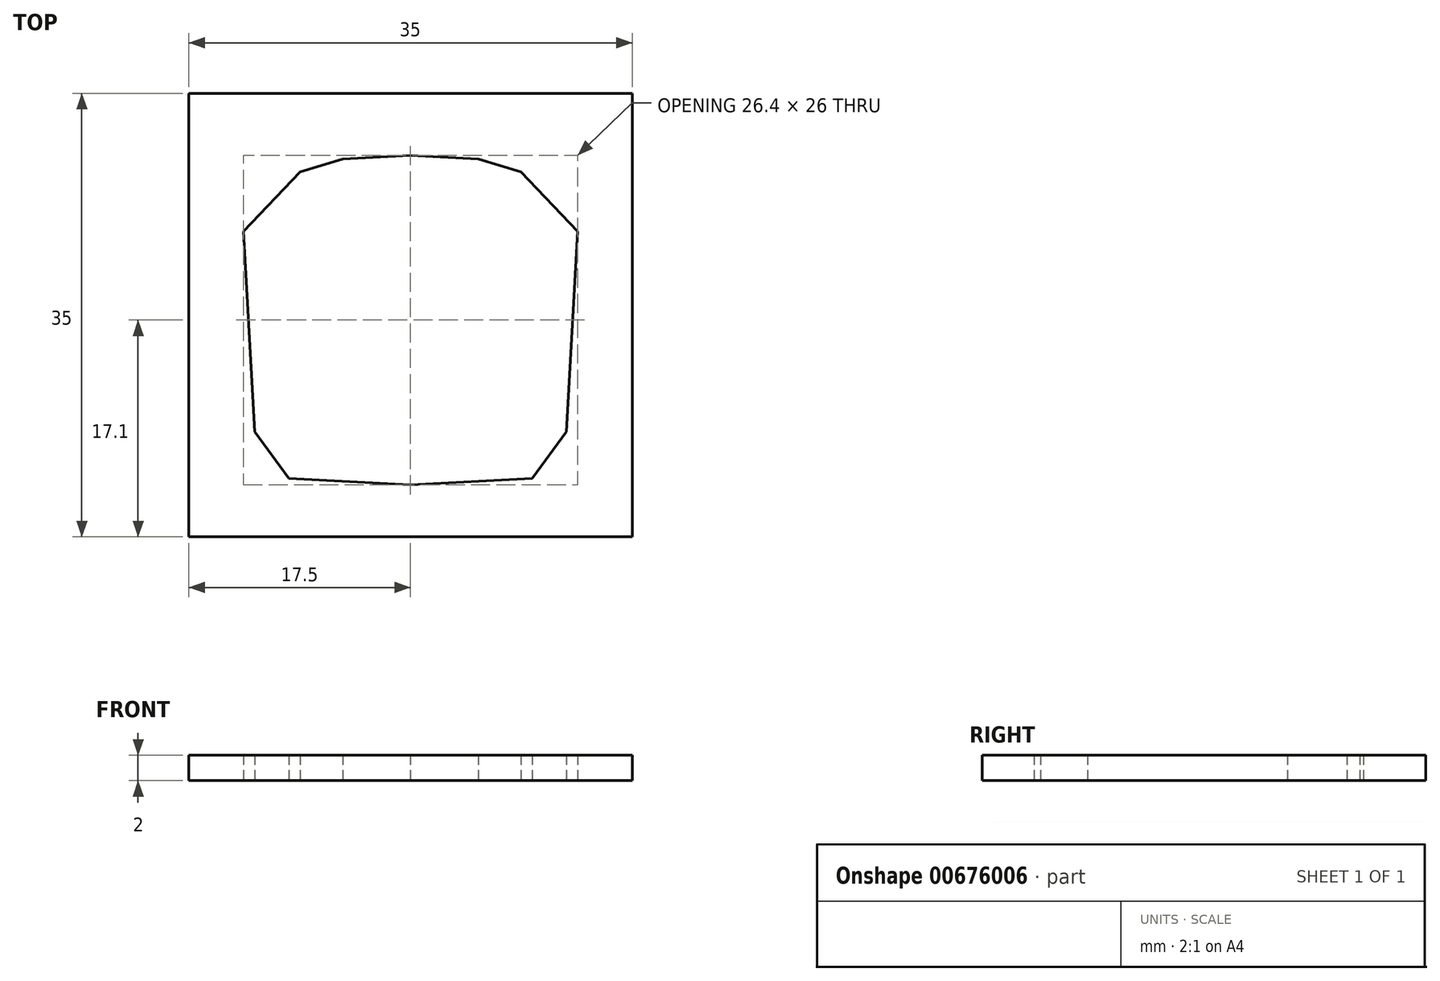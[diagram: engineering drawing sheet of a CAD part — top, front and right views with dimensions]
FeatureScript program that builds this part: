
annotation { "Feature Type Name" : "Feature", "Feature Type Description" : "" }
export const myFeature = defineFeature(function(context is Context, id is Id, definition is map)
    precondition{}
    {
        {
            var Q0;
            Q0=qCreatedBy(makeId("Top.planeOp"),FACE);
            var sketch = newSketch(context, id + "F0", { "sketchPlane" : qUnion([Q0])});
            skPoint(sketch, "E0", {"position": v(9.6, 0.5) * mm});
            skPoint(sketch, "E1", {"position": v(12.3, 4.2) * mm});
            skPoint(sketch, "E2", {"position": v(13.2, 20) * mm});
            skPoint(sketch, "E3", {"position": v(8.7, 24.7) * mm});
            skPoint(sketch, "E4", {"position": v(5.35, 25.7) * mm});
            skPoint(sketch, "E5", {"position": v(0, 26) * mm});
            skLineSegment(sketch, "E6", {"start": v(0, 0) * mm, "end": v(9.6, 0.5) * mm});
            skLineSegment(sketch, "E7", {"start": v(9.6, 0.5) * mm, "end": v(12.3, 4.2) * mm});
            skLineSegment(sketch, "E8", {"start": v(12.3, 4.2) * mm, "end": v(13.2, 20) * mm});
            skLineSegment(sketch, "E9", {"start": v(13.2, 20) * mm, "end": v(8.7, 24.7) * mm});
            skLineSegment(sketch, "E10", {"start": v(8.7, 24.7) * mm, "end": v(5.35, 25.7) * mm});
            skLineSegment(sketch, "E11", {"start": v(5.35, 25.7) * mm, "end": v(0, 26) * mm});
            skLineSegment(sketch, "E12.MirrorCS", {"start": v(-5.35, 25.7) * mm, "end": v(0, 26) * mm});
            skLineSegment(sketch, "E13.MirrorCS", {"start": v(-8.7, 24.7) * mm, "end": v(-5.35, 25.7) * mm});
            skLineSegment(sketch, "E14.MirrorCS", {"start": v(-13.2, 20) * mm, "end": v(-8.7, 24.7) * mm});
            skLineSegment(sketch, "E15.MirrorCS", {"start": v(-12.3, 4.2) * mm, "end": v(-13.2, 20) * mm});
            skLineSegment(sketch, "E16.MirrorCS", {"start": v(-9.6, 0.5) * mm, "end": v(-12.3, 4.2) * mm});
            skLineSegment(sketch, "E17.MirrorCS", {"start": v(0, 0) * mm, "end": v(-9.6, 0.5) * mm});
            skLineSegment(sketch, "E18", {"start": v(0, -4.1) * mm, "end": v(17.5, -4.1) * mm});
            skLineSegment(sketch, "E19", {"start": v(17.5, 30.9) * mm, "end": v(17.5, -4.1) * mm});
            skLineSegment(sketch, "E20", {"start": v(17.5, 30.9) * mm, "end": v(0, 30.9) * mm});
            skLineSegment(sketch, "E21.MirrorCS", {"start": v(-17.5, 30.9) * mm, "end": v(0, 30.9) * mm});
            skLineSegment(sketch, "E22.MirrorCS", {"start": v(-17.5, 30.9) * mm, "end": v(-17.5, -4.1) * mm});
            skLineSegment(sketch, "E23.MirrorCS", {"start": v(0, -4.1) * mm, "end": v(-17.5, -4.1) * mm});
            skSolve(sketch);
        }
        {
            var Q0;
            Q0=makeQuery(id+"F0.imprint","IMPRINT",FACE,{"disambiguationData":[TD([[makeQuery(id+"F0.imprint","IMPRINT",EDGE,{"derivedFrom":sQuery(id+"F0.wireOp",EDGE,"E6")}),-1.0]])]});
            extrude(context, id + "F1", {"entities" : qUnion([Q0]), "depth" : 2 * mm, "offsetDistance" : 25 * mm});
        }
    });
